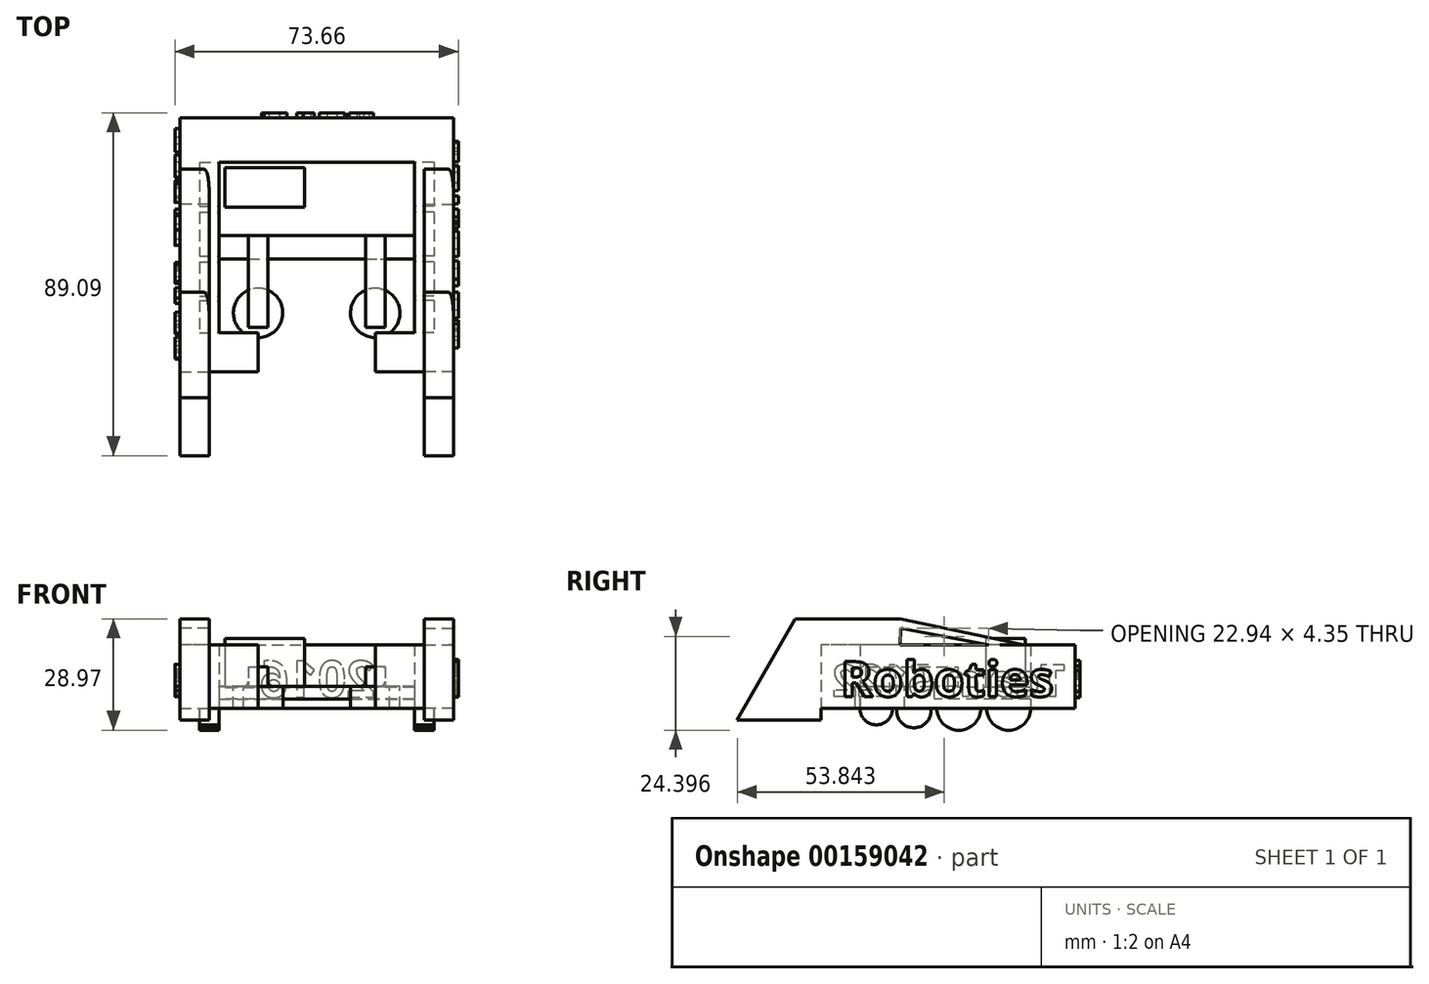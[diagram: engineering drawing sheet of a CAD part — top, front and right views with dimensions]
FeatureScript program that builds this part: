
annotation { "Feature Type Name" : "Feature", "Feature Type Description" : "" }
export const myFeature = defineFeature(function(context is Context, id is Id, definition is map)
    precondition{}
    {
        {
            var Q0;
            Q0=qCreatedBy(makeId("Top.planeOp"),FACE);
            var sketch = newSketch(context, id + "F0", { "sketchPlane" : qUnion([Q0])});
            skLineSegment(sketch, "E0.bottom", {"start": v(-25.4, 36.65) * mm, "end": v(25.4, 36.65) * mm});
            skLineSegment(sketch, "E0.top", {"start": v(-25.4, 25.1) * mm, "end": v(25.4, 25.1) * mm});
            skLineSegment(sketch, "E1.bottom", {"start": v(25.4, 36.65) * mm, "end": v(35.56, 36.65) * mm});
            skLineSegment(sketch, "E1.left", {"start": v(25.4, 25.1) * mm, "end": v(25.4, -19.23) * mm});
            skLineSegment(sketch, "E1.right", {"start": v(35.56, 36.65) * mm, "end": v(35.56, -19.23) * mm});
            skLineSegment(sketch, "E2.bottom", {"start": v(25.4, -19.23) * mm, "end": v(15.24, -19.23) * mm});
            skLineSegment(sketch, "E2.top", {"start": v(35.56, -29.4) * mm, "end": v(15.24, -29.4) * mm});
            skLineSegment(sketch, "E2.left", {"start": v(35.56, -19.23) * mm, "end": v(35.56, -29.4) * mm});
            skLineSegment(sketch, "E2.right", {"start": v(15.24, -19.23) * mm, "end": v(15.24, -29.4) * mm});
            skLineSegment(sketch, "E3.bottom", {"start": v(-25.4, 36.65) * mm, "end": v(-35.56, 36.65) * mm});
            skLineSegment(sketch, "E3.left", {"start": v(-25.4, 25.1) * mm, "end": v(-25.4, -19.23) * mm});
            skLineSegment(sketch, "E3.right", {"start": v(-35.56, 36.65) * mm, "end": v(-35.56, -19.23) * mm});
            skLineSegment(sketch, "E4.bottom", {"start": v(-25.4, -19.23) * mm, "end": v(-15.24, -19.23) * mm});
            skLineSegment(sketch, "E4.top", {"start": v(-35.56, -29.4) * mm, "end": v(-15.24, -29.4) * mm});
            skLineSegment(sketch, "E4.left", {"start": v(-35.56, -19.23) * mm, "end": v(-35.56, -29.4) * mm});
            skLineSegment(sketch, "E4.right", {"start": v(-15.24, -19.23) * mm, "end": v(-15.24, -29.4) * mm});
            skSolve(sketch);
        }
        {
            var Q0;
            Q0 = qSketchRegion(id + "F0", true);
            extrude(context, id + "F1", {"entities" : qUnion([Q0]), "depth" : 16.5 * mm});
        }
        {
            var Q0;
            Q0=makeQuery(id+"F1.opExtrude","SWEPT_FACE",FACE,{"disambiguationData":[OSD([sQuery(id+"F0.wireOp",EDGE,"E1.left")])]});
            var sketch = newSketch(context, id + "F2", { "sketchPlane" : qUnion([Q0])});
            skArc(sketch, "E5", {"start": v(-25.1, 0) * mm, "mid": v(-19.39, -5.72) * mm, "end": v(-13.67, 0) * mm});
            skArc(sketch, "E6.MirrorCS", {"start": v(-0.72, 0) * mm, "mid": v(-6.44, -5.72) * mm, "end": v(-12.15, 0) * mm});
            skArc(sketch, "E7", {"start": v(0.8, 0) * mm, "mid": v(5.25, -5.08) * mm, "end": v(9.7, 0) * mm});
            skArc(sketch, "E8", {"start": v(10.78, 0) * mm, "mid": v(15, -4.32) * mm, "end": v(19.23, 0) * mm});
            skLineSegment(sketch, "E9", {"start": v(-25.1, 0) * mm, "end": v(-13.67, 0) * mm});
            skLineSegment(sketch, "E10", {"start": v(0.8, 0) * mm, "end": v(9.7, 0) * mm});
            skLineSegment(sketch, "E11", {"start": v(10.78, 0) * mm, "end": v(19.23, 0) * mm});
            skLineSegment(sketch, "E12", {"start": v(-12.15, 0) * mm, "end": v(-0.72, 0) * mm});
            skSolve(sketch);
        }
        {
            var Q0;
            Q0 = qSketchRegion(id + "F2", true);
            extrude(context, id + "F3", {"entities" : qUnion([Q0]), "operationType" : NewBodyOperationType.ADD, "oppositeDirection" : true, "depth" : 5.08 * mm});
        }
        {
            var Q0;
            Q0=makeQuery(id+"F1.opExtrude","SWEPT_BODY",BODY,{"disambiguationData":[OSD([sQuery(id+"F0.wireOp",EDGE,"E0.bottom"),sQuery(id+"F0.wireOp",EDGE,"E0.top"),sQuery(id+"F0.wireOp",EDGE,"E1.bottom"),sQuery(id+"F0.wireOp",EDGE,"E1.left"),sQuery(id+"F0.wireOp",EDGE,"E1.right"),sQuery(id+"F0.wireOp",EDGE,"E2.bottom"),sQuery(id+"F0.wireOp",EDGE,"E2.top"),sQuery(id+"F0.wireOp",EDGE,"E2.left"),sQuery(id+"F0.wireOp",EDGE,"E2.right"),sQuery(id+"F0.wireOp",EDGE,"E3.bottom"),sQuery(id+"F0.wireOp",EDGE,"E3.left"),sQuery(id+"F0.wireOp",EDGE,"E3.right"),sQuery(id+"F0.wireOp",EDGE,"E4.bottom"),sQuery(id+"F0.wireOp",EDGE,"E4.top"),sQuery(id+"F0.wireOp",EDGE,"E4.left"),sQuery(id+"F0.wireOp",EDGE,"E4.right")])]});
            var Q1;
            Q1=qCreatedBy(makeId("Right.planeOp"),FACE);
            mirror(context, id + "F4", {"operationType" : NewBodyOperationType.ADD, "entities" : qUnion([Q0]), "mirrorPlane" : qUnion([Q1])});
        }
        {
            var Q0;
            Q0=makeQuery(id+"F1.opExtrude","SWEPT_FACE",FACE,{"disambiguationData":[OSD([sQuery(id+"F0.wireOp",EDGE,"E3.right"),sQuery(id+"F0.wireOp",EDGE,"E4.left")])]});
            var sketch = newSketch(context, id + "F5", { "sketchPlane" : qUnion([Q0])});
            skText(sketch, "E13", { "text": "Team 5122", "fontName": "OpenSans-Bold.ttf"});
            const initialGuessF5  = {"E13": [-0.0341, 0.00316, 1, 0, 0.00823]};
            skSetInitialGuess(sketch, initialGuessF5);
            skSolve(sketch);
        }
        {
            var Q0;
            Q0 = qSketchRegion(id + "F5", true);
            extrude(context, id + "F6", {"entities" : qUnion([Q0]), "operationType" : NewBodyOperationType.ADD, "depth" : 1.27 * mm});
        }
        {
            var Q0;
            Q0=makeQuery(id+"F1.opExtrude","SWEPT_FACE",FACE,{"disambiguationData":[OSD([sQuery(id+"F0.wireOp",EDGE,"E0.bottom"),sQuery(id+"F0.wireOp",EDGE,"E1.bottom"),sQuery(id+"F0.wireOp",EDGE,"E3.bottom")])]});
            var sketch = newSketch(context, id + "F7", { "sketchPlane" : qUnion([Q0])});
            skText(sketch, "E14", { "text": "2016", "fontName": "OpenSans-Bold.ttf"});
            const initialGuessF7  = {"E14": [-0.01524, 0.00288, 1, 0, 0.00947]};
            skSetInitialGuess(sketch, initialGuessF7);
            skSolve(sketch);
        }
        {
            var Q0;
            Q0 = qSketchRegion(id + "F7", true);
            extrude(context, id + "F8", {"entities" : qUnion([Q0]), "operationType" : NewBodyOperationType.ADD, "depth" : 1.27 * mm});
        }
        {
            var Q0;
            Q0=makeQuery(id+"F1.opExtrude","SWEPT_FACE",FACE,{"disambiguationData":[OSD([sQuery(id+"F0.wireOp",EDGE,"E1.right"),sQuery(id+"F0.wireOp",EDGE,"E2.left")])]});
            var sketch = newSketch(context, id + "F9", { "sketchPlane" : qUnion([Q0])});
            skText(sketch, "E15", { "text": "Roboties", "fontName": "OpenSans-Bold.ttf"});
            const initialGuessF9  = {"E15": [-0.02431, 0.00305, 1, 0, 0.00914]};
            skSetInitialGuess(sketch, initialGuessF9);
            skSolve(sketch);
        }
        {
            var Q0;
            Q0 = qSketchRegion(id + "F9", true);
            extrude(context, id + "F10", {"entities" : qUnion([Q0]), "operationType" : NewBodyOperationType.ADD, "depth" : 1.27 * mm});
        }
        {
            var Q0;
            Q0=makeQuery(id+"F1.opExtrude","SWEPT_FACE",FACE,{"disambiguationData":[OSD([sQuery(id+"F0.wireOp",EDGE,"E1.left")])]});
            var sketch = newSketch(context, id + "F11", { "sketchPlane" : qUnion([Q0])});
            skLineSegment(sketch, "E16.bottom", {"start": v(-6.11, 5.73) * mm, "end": v(0, 5.73) * mm});
            skLineSegment(sketch, "E16.top", {"start": v(-6.11, 2.43) * mm, "end": v(0, 2.43) * mm});
            skLineSegment(sketch, "E16.left", {"start": v(-6.11, 5.73) * mm, "end": v(-6.11, 2.43) * mm});
            skLineSegment(sketch, "E16.right", {"start": v(0, 5.73) * mm, "end": v(0, 2.43) * mm});
            skSolve(sketch);
        }
        {
            var Q0;
            Q0 = qSketchRegion(id + "F11", true);
            extrude(context, id + "F12", {"entities" : qUnion([Q0]), "operationType" : NewBodyOperationType.ADD, "depth" : 50.8 * mm});
        }
        {
            var Q0;
            Q0=makeQuery(id+"F12.opExtrude","SWEPT_FACE",FACE,{"disambiguationData":[OSD([sQuery(id+"F11.wireOp",EDGE,"E16.bottom")])]});
            var sketch = newSketch(context, id + "F13", { "sketchPlane" : qUnion([Q0])});
            skLineSegment(sketch, "E17", {"start": v(-17.76, -17.78) * mm, "end": v(-12.68, -17.78) * mm});
            skLineSegment(sketch, "E18.0.0", {"start": v(25.4, 0) * mm, "end": v(25.4, 6.11) * mm, "construction": true});
            skLineSegment(sketch, "E18.0.1", {"start": v(25.4, 6.11) * mm, "end": v(-25.4, 6.11) * mm, "construction": true});
            skLineSegment(sketch, "E18.0.2", {"start": v(-25.4, 6.11) * mm, "end": v(-25.4, 0) * mm, "construction": true});
            skLineSegment(sketch, "E18.0.3", {"start": v(-25.4, 0) * mm, "end": v(25.4, 0) * mm, "construction": true});
            skLineSegment(sketch, "E19", {"start": v(-17.78, 6.11) * mm, "end": v(-12.7, 6.11) * mm});
            skLineSegment(sketch, "E20", {"start": v(-17.76, -17.78) * mm, "end": v(-17.78, 6.11) * mm});
            skLineSegment(sketch, "E21", {"start": v(-12.68, -17.78) * mm, "end": v(-12.7, 6.11) * mm});
            skLineSegment(sketch, "E22", {"start": v(-12.7, 6.11) * mm, "end": v(-17.78, 6.11) * mm});
            skLineSegment(sketch, "E23", {"start": v(0, 6.11) * mm, "end": v(0, -18.1) * mm, "construction": true});
            skPoint(sketch, "E23.endSnap0", {"position": v(0, 6.11) * mm});
            skLineSegment(sketch, "E24.MirrorCS", {"start": v(17.76, -17.78) * mm, "end": v(17.78, 6.11) * mm});
            skLineSegment(sketch, "E25.MirrorCS", {"start": v(12.68, -17.78) * mm, "end": v(12.7, 6.11) * mm});
            skLineSegment(sketch, "E26.MirrorCS", {"start": v(17.76, -17.78) * mm, "end": v(12.68, -17.78) * mm});
            skLineSegment(sketch, "E27", {"start": v(12.7, 6.11) * mm, "end": v(17.78, 6.11) * mm});
            skSolve(sketch);
        }
        {
            var Q0;
            Q0 = qSketchRegion(id + "F13", true);
            extrude(context, id + "F14", {"entities" : qUnion([Q0]), "operationType" : NewBodyOperationType.ADD, "depth" : 5.08 * mm});
        }
        {
            var Q0;
            {var subQ0=sQuery(id+"F0.wireOp",EDGE,"E2.top");var subQ11=sQuery(id+"F0.wireOp",EDGE,"E2.left");var subQ13=sQuery(id+"F0.wireOp",EDGE,"E1.right");Q0=makeQuery(id+"F10.boolean.opBoolean","SPLIT",FACE,{"disambiguationData":[TD([makeQuery(id+"F1.opExtrude","SWEPT_FACE",FACE,{"disambiguationData":[OSD([subQ0])]})])],"derivedFrom":makeQuery(id+"F1.opExtrude","SWEPT_FACE",FACE,{"disambiguationData":[OSD([subQ13,subQ11])]})});}
            var sketch = newSketch(context, id + "F15", { "sketchPlane" : qUnion([Q0])});
            skLineSegment(sketch, "E28", {"start": v(-8.8, 16.51) * mm, "end": v(-29.4, 16.51) * mm});
            skLineSegment(sketch, "E29", {"start": v(-29.4, 16.51) * mm, "end": v(-29.4, -3.04) * mm});
            skLineSegment(sketch, "E30", {"start": v(-29.4, -3.04) * mm, "end": v(-51.17, -3.04) * mm});
            skLineSegment(sketch, "E31", {"start": v(-51.17, -3.04) * mm, "end": v(-36.13, 23.26) * mm});
            skLineSegment(sketch, "E32", {"start": v(-36.13, 23.26) * mm, "end": v(-8.7, 23.26) * mm});
            skLineSegment(sketch, "E33.0", {"start": v(36.65, 16.51) * mm, "end": v(-29.4, 16.51) * mm, "construction": true});
            skLineSegment(sketch, "E34", {"start": v(-8.7, 23.26) * mm, "end": v(23.31, 16.51) * mm});
            skLineSegment(sketch, "E35", {"start": v(23.31, 16.51) * mm, "end": v(14.14, 16.51) * mm});
            skLineSegment(sketch, "E36", {"start": v(14.14, 16.51) * mm, "end": v(-8.7, 20.86) * mm});
            skLineSegment(sketch, "E37", {"start": v(-8.7, 20.86) * mm, "end": v(-8.8, 16.51) * mm});
            skSolve(sketch);
        }
        {
            var Q0;
            Q0 = qSketchRegion(id + "F15", true);
            extrude(context, id + "F16", {"entities" : qUnion([Q0]), "oppositeDirection" : true, "depth" : 7.62 * mm});
        }
        {
            var Q0;
            Q0=makeQuery(id+"F16.opExtrude","SWEPT_BODY",BODY,{"disambiguationData":[OSD([sQuery(id+"F15.wireOp",EDGE,"E28"),sQuery(id+"F15.wireOp",EDGE,"E29"),sQuery(id+"F15.wireOp",EDGE,"E30"),sQuery(id+"F15.wireOp",EDGE,"E31"),sQuery(id+"F15.wireOp",EDGE,"E32"),sQuery(id+"F15.wireOp",EDGE,"f3TFiLgy-CstM-ECxc-FkMn-NOqoSjhTuX7e")])]});
            var Q1;
            Q1=qCreatedBy(makeId("Right.planeOp"),FACE);
            mirror(context, id + "F17", {"operationType" : NewBodyOperationType.ADD, "entities" : qUnion([Q0]), "mirrorPlane" : qUnion([Q1])});
        }
        {
            var Q0;
            Q0=makeQuery(id+"F16.opExtrude","CAP_EDGE",EDGE,{"disambiguationData":[OSD([sQuery(id+"F15.wireOp",EDGE,"E34")])],"isStart":true});
            var Q1;
            Q1=makeQuery(id+"F17.opPattern","COPY",EDGE,{"derivedFrom":makeQuery(id+"F16.opExtrude","CAP_EDGE",EDGE,{"disambiguationData":[OSD([sQuery(id+"F15.wireOp",EDGE,"E34")])],"isStart":false}),"instanceName":"1"});
            fillet(context, id + "F18", {"entities" : qUnion([Q0, Q1]), "radius" : 1.27 * mm, "tangentPropagation" : true, "allowEdgeOverflow" : false});
        }
        {
            var Q0;
            Q0=makeQuery(id+"F14.opExtrude","CAP_FACE",FACE,{"disambiguationData":[OSD([sQuery(id+"F13.wireOp",EDGE,"E17"),sQuery(id+"F13.wireOp",EDGE,"E20"),sQuery(id+"F13.wireOp",EDGE,"E21"),sQuery(id+"F13.wireOp",EDGE,"E19")])],"isStart":true});
            var sketch = newSketch(context, id + "F19", { "sketchPlane" : qUnion([Q0])});
            skLineSegment(sketch, "E38.0.0", {"start": v(-17.76, 17.78) * mm, "end": v(-17.77, 0) * mm, "construction": true});
            skLineSegment(sketch, "E38.0.1", {"start": v(-17.77, 0) * mm, "end": v(-12.7, 0) * mm, "construction": true});
            skLineSegment(sketch, "E38.0.2", {"start": v(-12.7, 0) * mm, "end": v(-12.68, 17.78) * mm, "construction": true});
            skLineSegment(sketch, "E38.0.3", {"start": v(-12.68, 17.78) * mm, "end": v(-17.76, 17.78) * mm, "construction": true});
            skLineSegment(sketch, "E39.0.0", {"start": v(12.68, 17.78) * mm, "end": v(12.7, 0) * mm, "construction": true});
            skLineSegment(sketch, "E39.0.1", {"start": v(12.7, 0) * mm, "end": v(17.77, 0) * mm, "construction": true});
            skLineSegment(sketch, "E39.0.2", {"start": v(17.77, 0) * mm, "end": v(17.76, 17.78) * mm, "construction": true});
            skLineSegment(sketch, "E39.0.3", {"start": v(17.76, 17.78) * mm, "end": v(12.68, 17.78) * mm, "construction": true});
            skLineSegment(sketch, "E40", {"start": v(0, 0) * mm, "end": v(0, 21.25) * mm, "construction": true});
            skLineSegment(sketch, "E41", {"start": v(15.22, 17.78) * mm, "end": v(15.22, 0) * mm, "construction": true});
            skCircle(sketch, "E42", {"center": v(15.22, 14.05) * mm, "radius": 6.42 * mm});
            skCircle(sketch, "E43.MirrorC", {"center": v(-15.22, 14.05) * mm, "radius": 6.42 * mm});
            skSolve(sketch);
        }
        {
            var Q0;
            Q0 = qSketchRegion(id + "F19", true);
            var Q1;
            Q1=makeQuery(id+"F1.opExtrude","CAP_FACE",FACE,{"disambiguationData":[OSD([sQuery(id+"F0.wireOp",EDGE,"E0.bottom"),sQuery(id+"F0.wireOp",EDGE,"E0.top"),sQuery(id+"F0.wireOp",EDGE,"E1.bottom"),sQuery(id+"F0.wireOp",EDGE,"E1.left"),sQuery(id+"F0.wireOp",EDGE,"E1.right"),sQuery(id+"F0.wireOp",EDGE,"E2.bottom"),sQuery(id+"F0.wireOp",EDGE,"E2.top"),sQuery(id+"F0.wireOp",EDGE,"E2.left"),sQuery(id+"F0.wireOp",EDGE,"E2.right"),sQuery(id+"F0.wireOp",EDGE,"E3.bottom"),sQuery(id+"F0.wireOp",EDGE,"E3.left"),sQuery(id+"F0.wireOp",EDGE,"E3.right"),sQuery(id+"F0.wireOp",EDGE,"E4.bottom"),sQuery(id+"F0.wireOp",EDGE,"E4.top"),sQuery(id+"F0.wireOp",EDGE,"E4.left"),sQuery(id+"F0.wireOp",EDGE,"E4.right")])],"isStart":true});
            extrude(context, id + "F20", {"entities" : qUnion([Q0]), "operationType" : NewBodyOperationType.ADD, "endBound" : BoundingType.UP_TO_SURFACE, "endBoundEntityFace" : qUnion([Q1]), "depth" : 25.4 * mm});
        }
        {
            var Q0;
            {var subQ0=sQuery(id+"F13.wireOp",EDGE,"E21");Q0=makeQuery(id+"F14.boolean.opBoolean","SPLIT",EDGE,{"disambiguationData":[topologyDisambiguationEdgeConnected([makeQuery(id+"F12.opExtrude","SWEPT_FACE",FACE,{"disambiguationData":[OSD([sQuery(id+"F11.wireOp",EDGE,"E16.bottom")])]})])],"derivedFrom":makeQuery(id+"F14.opExtrude","CAP_EDGE",EDGE,{"disambiguationData":[OSD([subQ0])],"isStart":true})});}
            var Q1;
            {var subQ0=sQuery(id+"F13.wireOp",EDGE,"E25.MirrorCS");Q1=makeQuery(id+"F14.boolean.opBoolean","SPLIT",EDGE,{"disambiguationData":[topologyDisambiguationEdgeConnected([makeQuery(id+"F12.opExtrude","SWEPT_FACE",FACE,{"disambiguationData":[OSD([sQuery(id+"F11.wireOp",EDGE,"E16.bottom")])]})])],"derivedFrom":makeQuery(id+"F14.opExtrude","CAP_EDGE",EDGE,{"disambiguationData":[OSD([subQ0])],"isStart":true})});}
            var Q2;
            {var subQ0=sQuery(id+"F13.wireOp",EDGE,"E24.MirrorCS");Q2=makeQuery(id+"F14.boolean.opBoolean","SPLIT",EDGE,{"disambiguationData":[topologyDisambiguationEdgeConnected([makeQuery(id+"F12.opExtrude","SWEPT_FACE",FACE,{"disambiguationData":[OSD([sQuery(id+"F11.wireOp",EDGE,"E16.bottom")])]})])],"derivedFrom":makeQuery(id+"F14.opExtrude","CAP_EDGE",EDGE,{"disambiguationData":[OSD([subQ0])],"isStart":true})});}
            var Q3;
            {var subQ0=sQuery(id+"F13.wireOp",EDGE,"E20");Q3=makeQuery(id+"F14.boolean.opBoolean","SPLIT",EDGE,{"disambiguationData":[topologyDisambiguationEdgeConnected([makeQuery(id+"F12.opExtrude","SWEPT_FACE",FACE,{"disambiguationData":[OSD([sQuery(id+"F11.wireOp",EDGE,"E16.bottom")])]})])],"derivedFrom":makeQuery(id+"F14.opExtrude","CAP_EDGE",EDGE,{"disambiguationData":[OSD([subQ0])],"isStart":true})});}
            fillet(context, id + "F21", {"entities" : qUnion([Q0, Q1, Q2, Q3]), "radius" : 1.27 * mm, "tangentPropagation" : true, "allowEdgeOverflow" : false});
        }
        {
            var Q0;
            Q0=makeQuery(id+"F4.boolean.opBoolean","MERGE",FACE,{"derivedFrom":[makeQuery(id+"F1.opExtrude","SWEPT_FACE",FACE,{"disambiguationData":[OSD([sQuery(id+"F0.wireOp",EDGE,"E3.left")])]}),makeQuery(id+"F4.opPattern","COPY",FACE,{"derivedFrom":makeQuery(id+"F3.boolean.opBoolean","MERGE",FACE,{"derivedFrom":[makeQuery(id+"F1.opExtrude","SWEPT_FACE",FACE,{"disambiguationData":[OSD([sQuery(id+"F0.wireOp",EDGE,"E1.left")])]}),makeQuery(id+"F3.opExtrude","CAP_FACE",FACE,{"disambiguationData":[OSD([sQuery(id+"F2.wireOp",EDGE,"E5"),sQuery(id+"F2.wireOp",EDGE,"E9")])],"isStart":true}),makeQuery(id+"F3.opExtrude","CAP_FACE",FACE,{"disambiguationData":[OSD([sQuery(id+"F2.wireOp",EDGE,"E6.MirrorCS"),sQuery(id+"F2.wireOp",EDGE,"E12")])],"isStart":true}),makeQuery(id+"F3.opExtrude","CAP_FACE",FACE,{"disambiguationData":[OSD([sQuery(id+"F2.wireOp",EDGE,"E7"),sQuery(id+"F2.wireOp",EDGE,"E10")])],"isStart":true}),makeQuery(id+"F3.opExtrude","CAP_FACE",FACE,{"disambiguationData":[OSD([sQuery(id+"F2.wireOp",EDGE,"E8"),sQuery(id+"F2.wireOp",EDGE,"E11")])],"isStart":true})]}),"instanceName":"1"})]});
            var sketch = newSketch(context, id + "F22", { "sketchPlane" : qUnion([Q0])});
            skLineSegment(sketch, "E44.0", {"start": v(6.11, 5.73) * mm, "end": v(6.11, 2.43) * mm, "construction": true});
            skLineSegment(sketch, "E45.0", {"start": v(25.1, 16.51) * mm, "end": v(25.1, 0) * mm, "construction": true});
            skLineSegment(sketch, "E46.bottom", {"start": v(6.11, 5.73) * mm, "end": v(25.1, 5.73) * mm});
            skLineSegment(sketch, "E46.top", {"start": v(6.11, 2.43) * mm, "end": v(25.1, 2.43) * mm});
            skLineSegment(sketch, "E46.left", {"start": v(6.11, 5.73) * mm, "end": v(6.11, 2.43) * mm});
            skLineSegment(sketch, "E46.right", {"start": v(25.1, 5.73) * mm, "end": v(25.1, 2.43) * mm});
            skSolve(sketch);
        }
        {
            var Q0;
            Q0 = qSketchRegion(id + "F22", true);
            var Q1;
            Q1=makeQuery(id+"F3.boolean.opBoolean","MERGE",FACE,{"derivedFrom":[makeQuery(id+"F1.opExtrude","SWEPT_FACE",FACE,{"disambiguationData":[OSD([sQuery(id+"F0.wireOp",EDGE,"E1.left")])]}),makeQuery(id+"F3.opExtrude","CAP_FACE",FACE,{"disambiguationData":[OSD([sQuery(id+"F2.wireOp",EDGE,"E5"),sQuery(id+"F2.wireOp",EDGE,"E9")])],"isStart":true}),makeQuery(id+"F3.opExtrude","CAP_FACE",FACE,{"disambiguationData":[OSD([sQuery(id+"F2.wireOp",EDGE,"E6.MirrorCS"),sQuery(id+"F2.wireOp",EDGE,"E12")])],"isStart":true}),makeQuery(id+"F3.opExtrude","CAP_FACE",FACE,{"disambiguationData":[OSD([sQuery(id+"F2.wireOp",EDGE,"E7"),sQuery(id+"F2.wireOp",EDGE,"E10")])],"isStart":true}),makeQuery(id+"F3.opExtrude","CAP_FACE",FACE,{"disambiguationData":[OSD([sQuery(id+"F2.wireOp",EDGE,"E8"),sQuery(id+"F2.wireOp",EDGE,"E11")])],"isStart":true})]});
            extrude(context, id + "F23", {"entities" : qUnion([Q0]), "operationType" : NewBodyOperationType.ADD, "endBound" : BoundingType.UP_TO_SURFACE, "endBoundEntityFace" : qUnion([Q1]), "depth" : 25.4 * mm});
        }
        {
            var Q0;
            {var subQ0=sQuery(id+"F13.wireOp",EDGE,"E21");var subQ12=makeQuery(id+"F12.opExtrude","SWEPT_FACE",FACE,{"disambiguationData":[OSD([sQuery(id+"F11.wireOp",EDGE,"E16.bottom")])]});var subQ17=makeQuery(id+"F1.opExtrude","SWEPT_FACE",FACE,{"disambiguationData":[OSD([sQuery(id+"F0.wireOp",EDGE,"E1.left")])]});Q0=makeQuery(id+"F23.boolean.opBoolean","MERGE",FACE,{"derivedFrom":[makeQuery(id+"F14.boolean.opBoolean","SPLIT",FACE,{"disambiguationData":[TD([subQ17])],"derivedFrom":subQ12}),makeQuery(id+"F14.boolean.opBoolean","SPLIT",FACE,{"disambiguationData":[TD([makeQuery(id+"F1.opExtrude","SWEPT_FACE",FACE,{"disambiguationData":[OSD([sQuery(id+"F0.wireOp",EDGE,"E3.left")])]})])],"derivedFrom":subQ12}),makeQuery(id+"F14.boolean.opBoolean","SPLIT",FACE,{"disambiguationData":[TD([makeQuery(id+"F14.opExtrude","SWEPT_FACE",FACE,{"disambiguationData":[OSD([subQ0])]})])],"derivedFrom":subQ12}),makeQuery(id+"F23.opExtrude","SWEPT_FACE",FACE,{"disambiguationData":[OSD([sQuery(id+"F22.wireOp",EDGE,"E46.bottom")])]})]});}
            var sketch = newSketch(context, id + "F24", { "sketchPlane" : qUnion([Q0])});
            skLineSegment(sketch, "E47.0.0", {"start": v(25.4, 0) * mm, "end": v(25.4, 25.1) * mm, "construction": true});
            skLineSegment(sketch, "E47.0.1", {"start": v(25.4, 25.1) * mm, "end": v(-25.4, 25.1) * mm, "construction": true});
            skLineSegment(sketch, "E47.0.2", {"start": v(-25.4, 25.1) * mm, "end": v(-25.4, 0) * mm, "construction": true});
            skLineSegment(sketch, "E47.0.3", {"start": v(-25.4, 0) * mm, "end": v(-19.04, 0) * mm, "construction": true});
            skLineSegment(sketch, "E47.0.4", {"start": v(-19.04, 0) * mm, "end": v(-19.05, 6.11) * mm, "construction": true});
            skLineSegment(sketch, "E47.0.5", {"start": v(-19.05, 6.11) * mm, "end": v(-11.43, 6.11) * mm, "construction": true});
            skLineSegment(sketch, "E47.0.6", {"start": v(-11.43, 6.11) * mm, "end": v(-11.42, 0) * mm, "construction": true});
            skLineSegment(sketch, "E47.0.7", {"start": v(-11.42, 0) * mm, "end": v(11.42, 0) * mm, "construction": true});
            skLineSegment(sketch, "E47.0.8", {"start": v(11.42, 0) * mm, "end": v(11.43, 6.11) * mm, "construction": true});
            skLineSegment(sketch, "E47.0.9", {"start": v(11.43, 6.11) * mm, "end": v(19.05, 6.11) * mm, "construction": true});
            skLineSegment(sketch, "E47.0.10", {"start": v(19.05, 6.11) * mm, "end": v(19.04, 0) * mm, "construction": true});
            skLineSegment(sketch, "E47.0.11", {"start": v(19.04, 0) * mm, "end": v(25.4, 0) * mm, "construction": true});
            skLineSegment(sketch, "E48.bottom", {"start": v(-25.4, 6.11) * mm, "end": v(25.4, 6.11) * mm});
            skLineSegment(sketch, "E48.top", {"start": v(-25.4, 25.1) * mm, "end": v(25.4, 25.1) * mm});
            skLineSegment(sketch, "E48.left", {"start": v(-25.4, 6.11) * mm, "end": v(-25.4, 25.1) * mm});
            skLineSegment(sketch, "E48.right", {"start": v(25.4, 6.11) * mm, "end": v(25.4, 25.1) * mm});
            skSolve(sketch);
        }
        {
            var Q0;
            Q0 = qSketchRegion(id + "F24", true);
            extrude(context, id + "F25", {"entities" : qUnion([Q0]), "operationType" : NewBodyOperationType.REMOVE, "oppositeDirection" : true, "depth" : 0.25 * mm});
        }
        {
            var Q0;
            Q0=makeQuery(id+"F25.boolean.opBoolean","COPY",FACE,{"derivedFrom":makeQuery(id+"F25.opExtrude","CAP_FACE",FACE,{"disambiguationData":[OSD([sQuery(id+"F24.wireOp",EDGE,"E48.bottom"),sQuery(id+"F24.wireOp",EDGE,"E48.top"),sQuery(id+"F24.wireOp",EDGE,"E48.left"),sQuery(id+"F24.wireOp",EDGE,"E48.right")])],"isStart":false})});
            var sketch = newSketch(context, id + "F26", { "sketchPlane" : qUnion([Q0])});
            skLineSegment(sketch, "E49.bottom", {"start": v(-23.8, 23.68) * mm, "end": v(-3.1, 23.68) * mm});
            skLineSegment(sketch, "E49.top", {"start": v(-23.8, 13.4) * mm, "end": v(-3.1, 13.4) * mm});
            skLineSegment(sketch, "E49.left", {"start": v(-23.8, 23.68) * mm, "end": v(-23.8, 13.4) * mm});
            skLineSegment(sketch, "E49.right", {"start": v(-3.1, 23.68) * mm, "end": v(-3.1, 13.4) * mm});
            skSolve(sketch);
        }
        {
            var Q0;
            Q0 = qSketchRegion(id + "F26", true);
            extrude(context, id + "F27", {"entities" : qUnion([Q0]), "operationType" : NewBodyOperationType.ADD, "depth" : 12.7 * mm});
        }
    });
